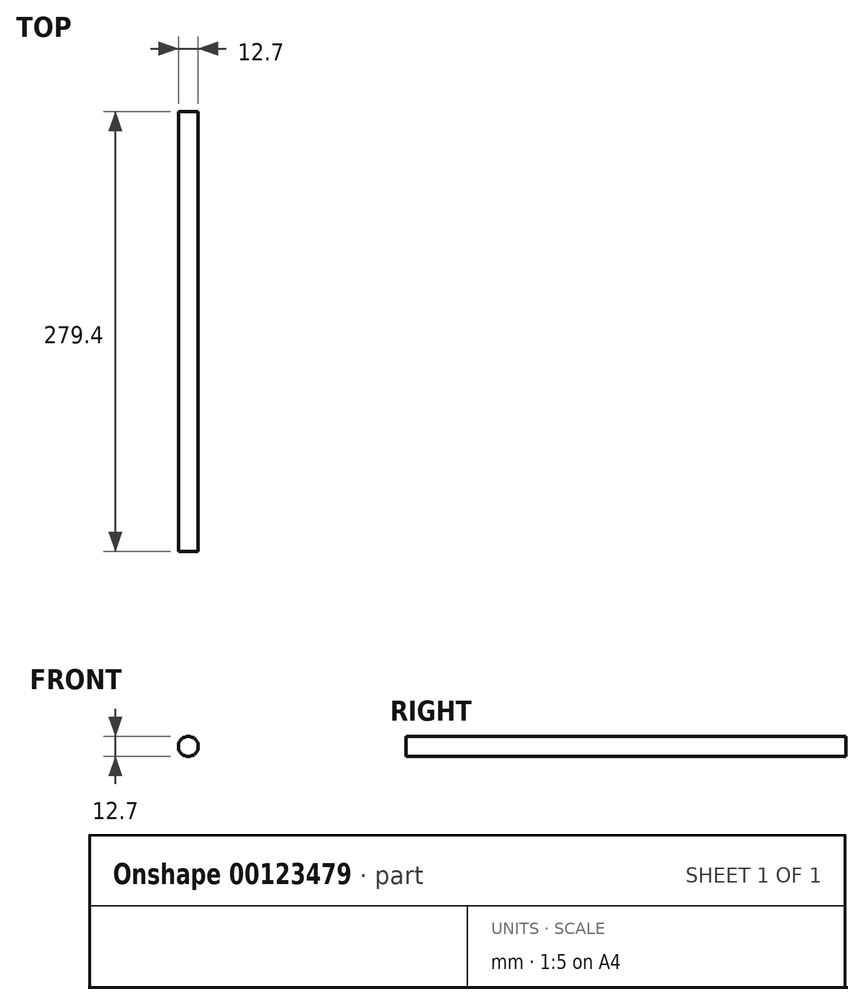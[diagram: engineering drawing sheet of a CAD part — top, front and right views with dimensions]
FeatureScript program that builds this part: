
annotation { "Feature Type Name" : "Feature", "Feature Type Description" : "" }
export const myFeature = defineFeature(function(context is Context, id is Id, definition is map)
    precondition{}
    {
        {
            var Q0;
            Q0=qCreatedBy(makeId("Front.planeOp"),FACE);
            var sketch = newSketch(context, id + "F0", { "sketchPlane" : qUnion([Q0])});
            skCircle(sketch, "E0", {"center": v(0, 0) * mm, "radius": 6.35 * mm});
            skSolve(sketch);
        }
        {
            var Q0;
            Q0=qSketchRegion(id+"F0",true);
            extrude(context, id + "F1", {"entities" : qUnion([Q0]), "endBound" : BoundingType.SYMMETRIC, "depth" : 279.4 * mm});
        }
    });
